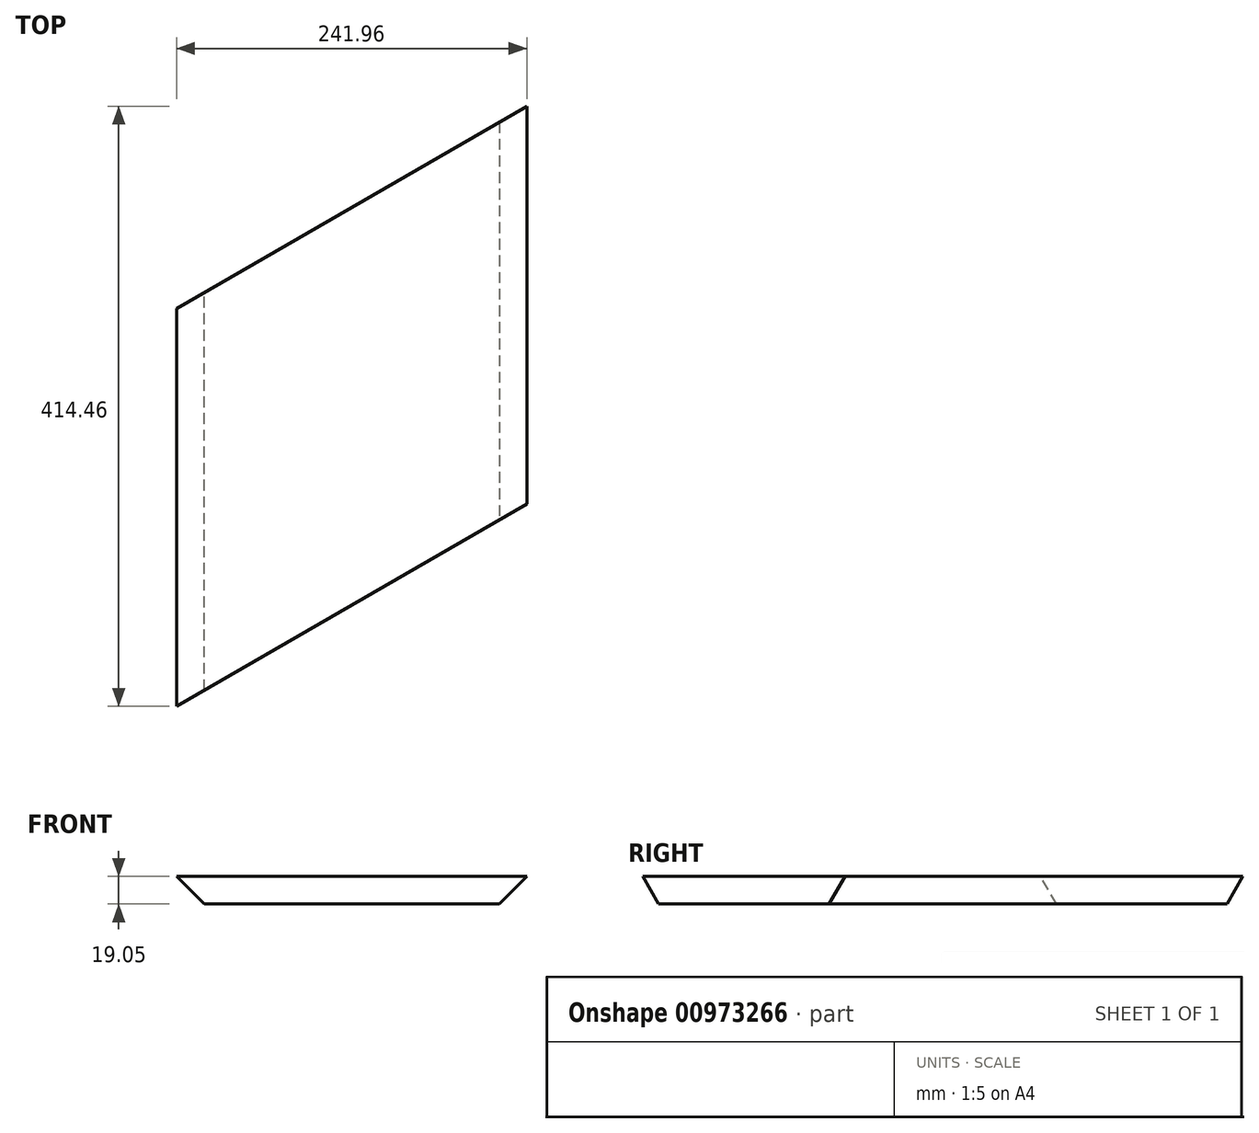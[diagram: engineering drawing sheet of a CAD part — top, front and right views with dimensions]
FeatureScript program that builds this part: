
annotation { "Feature Type Name" : "Feature", "Feature Type Description" : "" }
export const myFeature = defineFeature(function(context is Context, id is Id, definition is map)
    precondition{}
    {
        {
            var Q0;
            Q0=qCreatedBy(makeId("Top.planeOp"),FACE);
            var sketch = newSketch(context, id + "F0", { "sketchPlane" : qUnion([Q0])});
            skLineSegment(sketch, "E0.left", {"start": v(120.98, -67.53) * mm, "end": v(120.98, 207.23) * mm});
            skLineSegment(sketch, "E0.right", {"start": v(-120.98, -207.23) * mm, "end": v(-120.98, 67.53) * mm});
            skPoint(sketch, "E0.middle", {"position": v(0, 0) * mm});
            skLineSegment(sketch, "E1", {"start": v(-120.98, -207.23) * mm, "end": v(120.98, -67.53) * mm});
            skLineSegment(sketch, "E2", {"start": v(120.98, 207.23) * mm, "end": v(-120.98, 67.53) * mm});
            skPoint(sketch, "E3.orphan", {"position": v(-120.98, 248.36) * mm});
            skPoint(sketch, "E4.end.orphan", {"position": v(120.98, -248.36) * mm});
            skSolve(sketch);
        }
        {
            var Q0;
            Q0=qSketchRegion(id+"F0",true);
            extrude(context, id + "F1", {"entities" : qUnion([Q0]), "depth" : 19.05 * mm, "offsetDistance" : 25.4 * mm});
        }
        {
            var Q0;
            Q0=makeQuery(id+"F1.opExtrude","CAP_EDGE",EDGE,{"disambiguationData":[OSD([sQuery(id+"F0.wireOp",EDGE,"E0.right")])],"isStart":true});
            var Q1;
            Q1=makeQuery(id+"F1.opExtrude","CAP_EDGE",EDGE,{"disambiguationData":[OSD([sQuery(id+"F0.wireOp",EDGE,"E0.left")])],"isStart":true});
            chamfer(context, id + "F2", {"entities" : qUnion([Q0, Q1]), "width" : 19.05 * mm, "tangentPropagation" : true});
        }
    });
